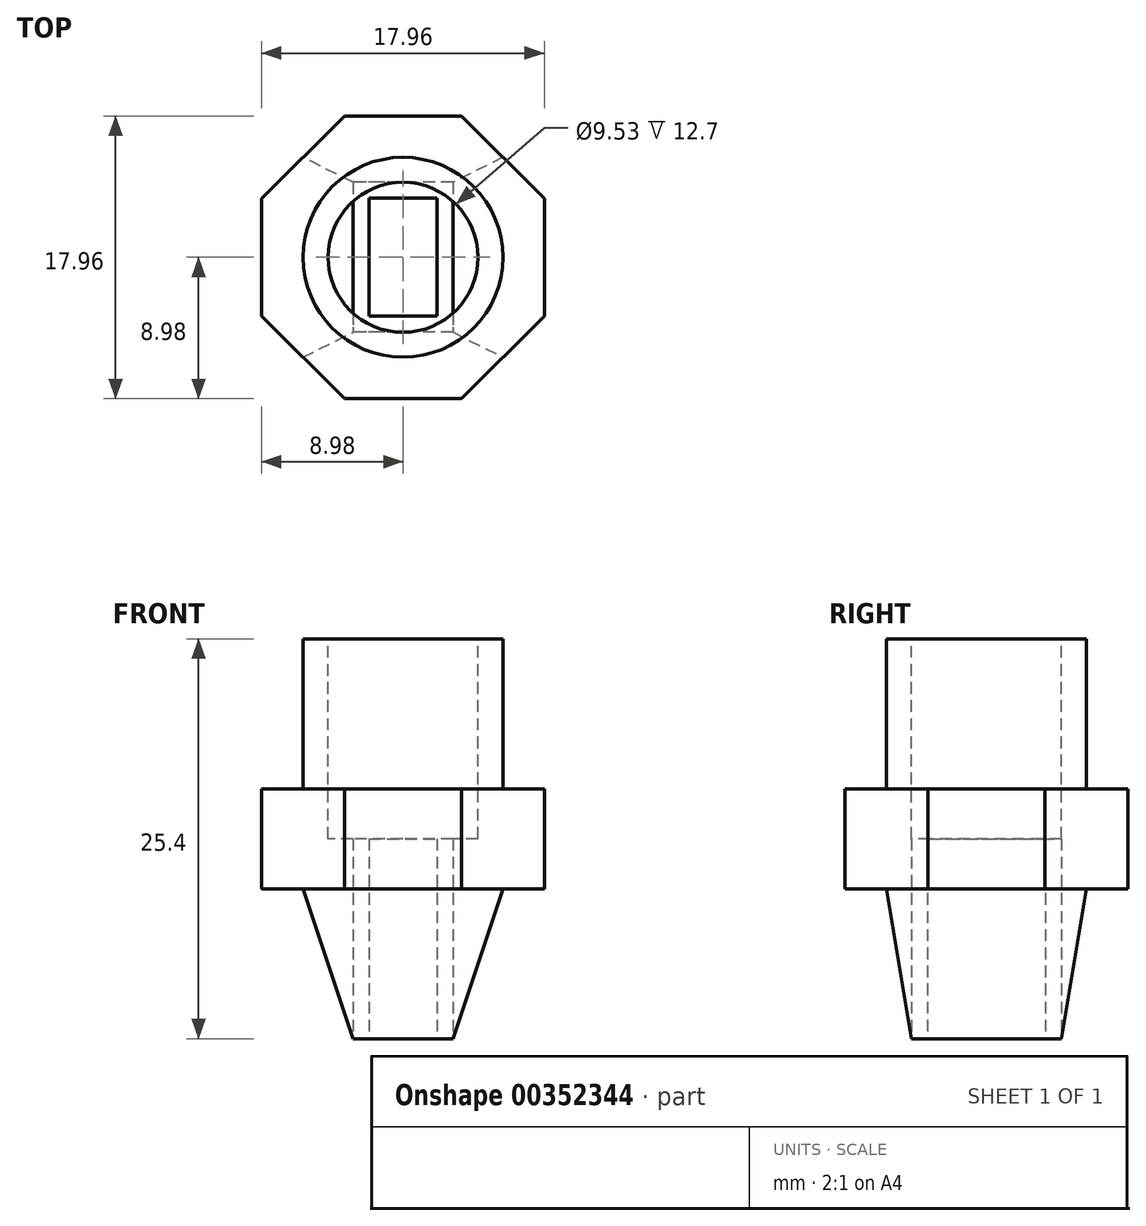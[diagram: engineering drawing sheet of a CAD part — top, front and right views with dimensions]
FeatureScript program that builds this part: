
annotation { "Feature Type Name" : "Feature", "Feature Type Description" : "" }
export const myFeature = defineFeature(function(context is Context, id is Id, definition is map)
    precondition{}
    {
        {
            var Q0;
            Q0=qCreatedBy(makeId("Top.planeOp"),FACE);
            var sketch = newSketch(context, id + "F0", { "sketchPlane" : qUnion([Q0])});
            skLineSegment(sketch, "E0.bottom", {"start": v(0, 0) * mm, "end": v(12.7, 0) * mm});
            skLineSegment(sketch, "E0.top", {"start": v(0, 12.7) * mm, "end": v(12.7, 12.7) * mm});
            skLineSegment(sketch, "E0.left", {"start": v(0, 0) * mm, "end": v(0, 12.7) * mm});
            skLineSegment(sketch, "E0.right", {"start": v(12.7, 0) * mm, "end": v(12.7, 12.7) * mm});
            skSolve(sketch);
        }
        {
            var Q0;
            Q0 = qSketchRegion(id + "F0", true);
            extrude(context, id + "F1", {"entities" : qUnion([Q0]), "depth" : 25.4 * mm});
        }
        {
            var Q0;
            Q0=makeQuery(id+"F1.opExtrude","SWEPT_FACE",FACE,{"disambiguationData":[OSD([sQuery(id+"F0.wireOp",EDGE,"E0.bottom")])]});
            var sketch = newSketch(context, id + "F2", { "sketchPlane" : qUnion([Q0])});
            skLineSegment(sketch, "E1", {"start": v(3.18, 0) * mm, "end": v(0, 9.53) * mm});
            skLineSegment(sketch, "E2", {"start": v(0, 9.53) * mm, "end": v(12.7, 9.53) * mm, "construction": true});
            skLineSegment(sketch, "E3", {"start": v(12.7, 9.53) * mm, "end": v(9.53, 0) * mm});
            skLineSegment(sketch, "E4", {"start": v(0, 0) * mm, "end": v(3.18, 0) * mm});
            skLineSegment(sketch, "E5", {"start": v(9.53, 0) * mm, "end": v(12.7, 0) * mm});
            skLineSegment(sketch, "E6", {"start": v(0, 9.53) * mm, "end": v(0, 0) * mm});
            skLineSegment(sketch, "E7", {"start": v(12.7, 0) * mm, "end": v(12.7, 9.53) * mm});
            skSolve(sketch);
        }
        {
            var Q0;
            Q0 = qSketchRegion(id + "F2", true);
            extrude(context, id + "F3", {"entities" : qUnion([Q0]), "operationType" : NewBodyOperationType.REMOVE, "endBound" : BoundingType.THROUGH_ALL, "oppositeDirection" : true, "depth" : 25.4 * mm});
        }
        {
            var Q0;
            Q0=makeQuery(id+"F1.opExtrude","SWEPT_FACE",FACE,{"disambiguationData":[OSD([sQuery(id+"F0.wireOp",EDGE,"E0.left")])]});
            var sketch = newSketch(context, id + "F4", { "sketchPlane" : qUnion([Q0])});
            skLineSegment(sketch, "E8", {"start": v(-12.7, 9.53) * mm, "end": v(-11.11, 0) * mm});
            skLineSegment(sketch, "E9", {"start": v(-11.11, 0) * mm, "end": v(-12.7, 0) * mm});
            skLineSegment(sketch, "E10", {"start": v(-12.7, 0) * mm, "end": v(-12.7, 9.53) * mm});
            skLineSegment(sketch, "E11", {"start": v(0, 9.53) * mm, "end": v(0, 0) * mm});
            skLineSegment(sketch, "E12", {"start": v(0, 0) * mm, "end": v(-1.59, 0) * mm});
            skLineSegment(sketch, "E13", {"start": v(-1.59, 0) * mm, "end": v(0, 9.53) * mm});
            skSolve(sketch);
        }
        {
            var Q0;
            Q0 = qSketchRegion(id + "F4", true);
            extrude(context, id + "F5", {"entities" : qUnion([Q0]), "operationType" : NewBodyOperationType.REMOVE, "endBound" : BoundingType.THROUGH_ALL, "oppositeDirection" : true, "depth" : 25.4 * mm});
        }
        {
            var Q0;
            Q0=makeQuery(id+"F1.opExtrude","CAP_FACE",FACE,{"disambiguationData":[OSD([sQuery(id+"F0.wireOp",EDGE,"E0.bottom"),sQuery(id+"F0.wireOp",EDGE,"E0.top"),sQuery(id+"F0.wireOp",EDGE,"E0.left"),sQuery(id+"F0.wireOp",EDGE,"E0.right")])],"isStart":true});
            var sketch = newSketch(context, id + "F6", { "sketchPlane" : qUnion([Q0])});
            skLineSegment(sketch, "E14.bottom", {"start": v(4.2, -2.6) * mm, "end": v(8.5, -2.6) * mm});
            skLineSegment(sketch, "E14.top", {"start": v(4.2, -10.1) * mm, "end": v(8.5, -10.1) * mm});
            skLineSegment(sketch, "E14.left", {"start": v(4.2, -2.6) * mm, "end": v(4.2, -10.1) * mm});
            skLineSegment(sketch, "E14.right", {"start": v(8.5, -2.6) * mm, "end": v(8.5, -10.1) * mm});
            skLineSegment(sketch, "E15.bottom", {"start": v(9.52, -11.11) * mm, "end": v(3.18, -11.11) * mm});
            skLineSegment(sketch, "E15.top", {"start": v(9.52, -1.59) * mm, "end": v(3.18, -1.59) * mm});
            skLineSegment(sketch, "E15.left", {"start": v(9.52, -11.11) * mm, "end": v(9.52, -1.59) * mm});
            skLineSegment(sketch, "E15.right", {"start": v(3.18, -11.11) * mm, "end": v(3.18, -1.59) * mm});
            skSolve(sketch);
        }
        {
            var Q0;
            Q0 = qSketchRegion(id + "F6", true);
            extrude(context, id + "F7", {"entities" : qUnion([Q0]), "operationType" : NewBodyOperationType.REMOVE, "endBound" : BoundingType.THROUGH_ALL, "oppositeDirection" : true, "depth" : 25.4 * mm});
        }
        {
            var Q0;
            Q0=makeQuery(id+"F7.boolean.opBoolean","SPLIT",FACE,{"disambiguationData":[TD([makeQuery(id+"F7.opExtrude","SWEPT_FACE",FACE,{"disambiguationData":[OSD([sQuery(id+"F6.wireOp",EDGE,"E14.bottom")])]})])],"derivedFrom":makeQuery(id+"F1.opExtrude","CAP_FACE",FACE,{"disambiguationData":[OSD([sQuery(id+"F0.wireOp",EDGE,"E0.bottom"),sQuery(id+"F0.wireOp",EDGE,"E0.top"),sQuery(id+"F0.wireOp",EDGE,"E0.left"),sQuery(id+"F0.wireOp",EDGE,"E0.right")])],"isStart":false})});
            var sketch = newSketch(context, id + "F8", { "sketchPlane" : qUnion([Q0])});
            skLineSegment(sketch, "E16", {"start": v(4.2, 10.1) * mm, "end": v(8.5, 2.6) * mm, "construction": true});
            skLineSegment(sketch, "E17", {"start": v(4.2, 2.6) * mm, "end": v(8.5, 10.1) * mm, "construction": true});
            skCircle(sketch, "E18.cCircle", {"center": v(6.35, 6.35) * mm, "radius": 8.98 * mm, "construction": true});
            skLineSegment(sketch, "E18.0", {"start": v(2.63, 15.33) * mm, "end": v(10.07, 15.33) * mm});
            skLineSegment(sketch, "E18.1", {"start": v(10.07, 15.33) * mm, "end": v(15.33, 10.07) * mm});
            skLineSegment(sketch, "E18.2", {"start": v(15.33, 10.07) * mm, "end": v(15.33, 2.63) * mm});
            skLineSegment(sketch, "E18.3", {"start": v(15.33, 2.63) * mm, "end": v(10.07, -2.63) * mm});
            skLineSegment(sketch, "E18.4", {"start": v(10.07, -2.63) * mm, "end": v(2.63, -2.63) * mm});
            skLineSegment(sketch, "E18.5", {"start": v(2.63, -2.63) * mm, "end": v(-2.63, 2.63) * mm});
            skLineSegment(sketch, "E18.6", {"start": v(-2.63, 2.63) * mm, "end": v(-2.63, 10.07) * mm});
            skLineSegment(sketch, "E18.7", {"start": v(-2.63, 10.07) * mm, "end": v(2.63, 15.33) * mm});
            skPoint(sketch, "E18.0.midPoint", {"position": v(6.35, 15.33) * mm});
            skLineSegment(sketch, "E19.bottom", {"start": v(0, 12.7) * mm, "end": v(12.7, 12.7) * mm});
            skLineSegment(sketch, "E19.top", {"start": v(0, 0) * mm, "end": v(12.7, 0) * mm});
            skLineSegment(sketch, "E19.left", {"start": v(0, 12.7) * mm, "end": v(0, 0) * mm});
            skLineSegment(sketch, "E19.right", {"start": v(12.7, 12.7) * mm, "end": v(12.7, 0) * mm});
            skSolve(sketch);
        }
        {
            var Q0;
            {var subQ0=sQuery(id+"F8.wireOp",EDGE,"E18.6");Q0=makeQuery(id+"F8.imprint","IMPRINT",FACE,{"disambiguationData":[TD([[makeQuery(id+"F8.imprint","IMPRINT",EDGE,{"derivedFrom":subQ0}),-1.0]])]});}
            var Q1;
            {var subQ0=sQuery(id+"F8.wireOp",EDGE,"E18.0");Q1=makeQuery(id+"F8.imprint","IMPRINT",FACE,{"disambiguationData":[TD([[makeQuery(id+"F8.imprint","IMPRINT",EDGE,{"derivedFrom":subQ0}),-1.0]])]});}
            var Q2;
            {var subQ0=sQuery(id+"F8.wireOp",EDGE,"E18.2");Q2=makeQuery(id+"F8.imprint","IMPRINT",FACE,{"disambiguationData":[TD([[makeQuery(id+"F8.imprint","IMPRINT",EDGE,{"derivedFrom":subQ0}),-1.0]])]});}
            var Q3;
            {var subQ0=sQuery(id+"F8.wireOp",EDGE,"E18.4");Q3=makeQuery(id+"F8.imprint","IMPRINT",FACE,{"disambiguationData":[TD([[makeQuery(id+"F8.imprint","IMPRINT",EDGE,{"derivedFrom":subQ0}),-1.0]])]});}
            extrude(context, id + "F9", {"entities" : qUnion([Q0, Q1, Q2, Q3]), "operationType" : NewBodyOperationType.ADD, "oppositeDirection" : true, "depth" : 15.88 * mm});
        }
        {
            var Q0;
            {var subQ0=sQuery(id+"F8.wireOp",EDGE,"E18.7");var subQ1=sQuery(id+"F8.wireOp",EDGE,"E18.5");var subQ2=sQuery(id+"F8.wireOp",EDGE,"E18.3");var subQ3=sQuery(id+"F8.wireOp",EDGE,"E18.1");var subQ4=sQuery(id+"F0.wireOp",EDGE,"E0.left");var subQ5=sQuery(id+"F0.wireOp",EDGE,"E0.top");var subQ6=sQuery(id+"F0.wireOp",EDGE,"E0.right");var subQ7=sQuery(id+"F0.wireOp",EDGE,"E0.bottom");Q0=makeQuery(id+"F9.boolean.opBoolean","MERGE",FACE,{"derivedFrom":[makeQuery(id+"F7.boolean.opBoolean","SPLIT",FACE,{"disambiguationData":[TD([makeQuery(id+"F1.opExtrude","SWEPT_FACE",FACE,{"disambiguationData":[OSD([subQ7])]})])],"derivedFrom":makeQuery(id+"F1.opExtrude","CAP_FACE",FACE,{"disambiguationData":[OSD([subQ7,subQ5,subQ4,subQ6])],"isStart":false})}),makeQuery(id+"F9.opExtrude","CAP_FACE",FACE,{"disambiguationData":[OSD([sQuery(id+"F8.wireOp",EDGE,"E18.0"),subQ3,subQ0,sQuery(id+"F8.wireOp",EDGE,"E19.bottom")])],"isStart":true}),makeQuery(id+"F9.opExtrude","CAP_FACE",FACE,{"disambiguationData":[OSD([subQ3,sQuery(id+"F8.wireOp",EDGE,"E18.2"),subQ2,sQuery(id+"F8.wireOp",EDGE,"E19.right")])],"isStart":true}),makeQuery(id+"F9.opExtrude","CAP_FACE",FACE,{"disambiguationData":[OSD([subQ2,sQuery(id+"F8.wireOp",EDGE,"E18.4"),subQ1,sQuery(id+"F8.wireOp",EDGE,"E19.top")])],"isStart":true}),makeQuery(id+"F9.opExtrude","CAP_FACE",FACE,{"disambiguationData":[OSD([subQ1,sQuery(id+"F8.wireOp",EDGE,"E18.6"),subQ0,sQuery(id+"F8.wireOp",EDGE,"E19.left")])],"isStart":true})]});}
            var sketch = newSketch(context, id + "F10", { "sketchPlane" : qUnion([Q0])});
            skLineSegment(sketch, "E20.0", {"start": v(-2.63, 10.07) * mm, "end": v(2.63, 15.33) * mm});
            skLineSegment(sketch, "E21.0", {"start": v(2.63, 15.33) * mm, "end": v(10.07, 15.33) * mm});
            skLineSegment(sketch, "E22.0", {"start": v(10.07, 15.33) * mm, "end": v(15.33, 10.07) * mm});
            skLineSegment(sketch, "E23.0", {"start": v(-2.63, 2.63) * mm, "end": v(-2.63, 10.07) * mm});
            skLineSegment(sketch, "E24.0", {"start": v(2.63, -2.63) * mm, "end": v(-2.63, 2.63) * mm});
            skLineSegment(sketch, "E25.0", {"start": v(10.07, -2.63) * mm, "end": v(2.63, -2.63) * mm});
            skLineSegment(sketch, "E26.0", {"start": v(15.33, 2.63) * mm, "end": v(10.07, -2.63) * mm});
            skLineSegment(sketch, "E27.0", {"start": v(15.33, 10.07) * mm, "end": v(15.33, 2.63) * mm});
            skCircle(sketch, "E28", {"center": v(6.35, 6.35) * mm, "radius": 6.35 * mm});
            skLineSegment(sketch, "E29", {"start": v(3.17, 11.11) * mm, "end": v(9.53, 1.59) * mm, "construction": true});
            skLineSegment(sketch, "E30", {"start": v(9.52, 11.11) * mm, "end": v(3.18, 1.59) * mm, "construction": true});
            skSolve(sketch);
        }
        {
            var Q0;
            {var subQ0=sQuery(id+"F10.wireOp",EDGE,"E24.0");var subQ1=sQuery(id+"F10.wireOp",EDGE,"E23.0");var subQ2=makeQuery(id+"F10.imprint","INTERSECT",VERTEX,{"derivedFrom":[subQ1,subQ0]});Q0=makeQuery(id+"F10.imprint","IMPRINT",FACE,{"disambiguationData":[TD([[makeQuery(id+"F10.imprint","IMPRINT",EDGE,{"disambiguationData":[TD([[subQ2,-1.0]])],"derivedFrom":subQ1}),-1.0]])]});}
            var Q1;
            {var subQ0=sQuery(id+"F10.wireOp",EDGE,"E25.0");var subQ1=sQuery(id+"F10.wireOp",EDGE,"E24.0");var subQ2=makeQuery(id+"F10.imprint","INTERSECT",VERTEX,{"derivedFrom":[subQ1,subQ0]});Q1=makeQuery(id+"F10.imprint","IMPRINT",FACE,{"disambiguationData":[TD([[makeQuery(id+"F10.imprint","IMPRINT",EDGE,{"disambiguationData":[TD([[subQ2,-1.0]])],"derivedFrom":subQ1}),-1.0]])]});}
            var Q2;
            {var subQ0=sQuery(id+"F10.wireOp",EDGE,"E26.0");var subQ1=sQuery(id+"F10.wireOp",EDGE,"E25.0");var subQ2=makeQuery(id+"F10.imprint","INTERSECT",VERTEX,{"derivedFrom":[subQ1,subQ0]});Q2=makeQuery(id+"F10.imprint","IMPRINT",FACE,{"disambiguationData":[TD([[makeQuery(id+"F10.imprint","IMPRINT",EDGE,{"disambiguationData":[TD([[subQ2,-1.0]])],"derivedFrom":subQ1}),-1.0]])]});}
            var Q3;
            {var subQ0=sQuery(id+"F10.wireOp",EDGE,"E27.0");var subQ1=sQuery(id+"F10.wireOp",EDGE,"E26.0");var subQ2=makeQuery(id+"F10.imprint","INTERSECT",VERTEX,{"derivedFrom":[subQ1,subQ0]});Q3=makeQuery(id+"F10.imprint","IMPRINT",FACE,{"disambiguationData":[TD([[makeQuery(id+"F10.imprint","IMPRINT",EDGE,{"disambiguationData":[TD([[subQ2,-1.0]])],"derivedFrom":subQ1}),-1.0]])]});}
            var Q4;
            {var subQ0=sQuery(id+"F10.wireOp",EDGE,"E27.0");var subQ1=sQuery(id+"F10.wireOp",EDGE,"E22.0");var subQ2=makeQuery(id+"F10.imprint","INTERSECT",VERTEX,{"derivedFrom":[subQ1,subQ0]});Q4=makeQuery(id+"F10.imprint","IMPRINT",FACE,{"disambiguationData":[TD([[makeQuery(id+"F10.imprint","IMPRINT",EDGE,{"disambiguationData":[TD([[subQ2,1.0]])],"derivedFrom":subQ1}),-1.0]])]});}
            var Q5;
            {var subQ0=sQuery(id+"F10.wireOp",EDGE,"E22.0");var subQ1=sQuery(id+"F10.wireOp",EDGE,"E21.0");var subQ2=makeQuery(id+"F10.imprint","INTERSECT",VERTEX,{"derivedFrom":[subQ1,subQ0]});Q5=makeQuery(id+"F10.imprint","IMPRINT",FACE,{"disambiguationData":[TD([[makeQuery(id+"F10.imprint","IMPRINT",EDGE,{"disambiguationData":[TD([[subQ2,1.0]])],"derivedFrom":subQ1}),-1.0]])]});}
            var Q6;
            {var subQ0=sQuery(id+"F10.wireOp",EDGE,"E21.0");var subQ1=sQuery(id+"F10.wireOp",EDGE,"E20.0");var subQ2=makeQuery(id+"F10.imprint","INTERSECT",VERTEX,{"derivedFrom":[subQ1,subQ0]});Q6=makeQuery(id+"F10.imprint","IMPRINT",FACE,{"disambiguationData":[TD([[makeQuery(id+"F10.imprint","IMPRINT",EDGE,{"disambiguationData":[TD([[subQ2,1.0]])],"derivedFrom":subQ1}),-1.0]])]});}
            var Q7;
            {var subQ0=sQuery(id+"F10.wireOp",EDGE,"E23.0");var subQ1=sQuery(id+"F10.wireOp",EDGE,"E20.0");var subQ2=makeQuery(id+"F10.imprint","INTERSECT",VERTEX,{"derivedFrom":[subQ1,subQ0]});Q7=makeQuery(id+"F10.imprint","IMPRINT",FACE,{"disambiguationData":[TD([[makeQuery(id+"F10.imprint","IMPRINT",EDGE,{"disambiguationData":[TD([[subQ2,-1.0]])],"derivedFrom":subQ1}),-1.0]])]});}
            extrude(context, id + "F11", {"entities" : qUnion([Q0, Q1, Q2, Q3, Q4, Q5, Q6, Q7]), "operationType" : NewBodyOperationType.REMOVE, "oppositeDirection" : true, "depth" : 9.52 * mm});
        }
        {
            var Q0;
            {var subQ0=sQuery(id+"F8.wireOp",EDGE,"E18.7");var subQ1=sQuery(id+"F8.wireOp",EDGE,"E18.5");var subQ2=sQuery(id+"F8.wireOp",EDGE,"E18.3");var subQ3=sQuery(id+"F8.wireOp",EDGE,"E18.1");var subQ4=sQuery(id+"F0.wireOp",EDGE,"E0.left");var subQ5=sQuery(id+"F0.wireOp",EDGE,"E0.top");var subQ6=sQuery(id+"F0.wireOp",EDGE,"E0.right");var subQ7=sQuery(id+"F0.wireOp",EDGE,"E0.bottom");Q0=makeQuery(id+"F9.boolean.opBoolean","MERGE",FACE,{"derivedFrom":[makeQuery(id+"F7.boolean.opBoolean","SPLIT",FACE,{"disambiguationData":[TD([makeQuery(id+"F1.opExtrude","SWEPT_FACE",FACE,{"disambiguationData":[OSD([subQ7])]})])],"derivedFrom":makeQuery(id+"F1.opExtrude","CAP_FACE",FACE,{"disambiguationData":[OSD([subQ7,subQ5,subQ4,subQ6])],"isStart":false})}),makeQuery(id+"F9.opExtrude","CAP_FACE",FACE,{"disambiguationData":[OSD([sQuery(id+"F8.wireOp",EDGE,"E18.0"),subQ3,subQ0,sQuery(id+"F8.wireOp",EDGE,"E19.bottom")])],"isStart":true}),makeQuery(id+"F9.opExtrude","CAP_FACE",FACE,{"disambiguationData":[OSD([subQ3,sQuery(id+"F8.wireOp",EDGE,"E18.2"),subQ2,sQuery(id+"F8.wireOp",EDGE,"E19.right")])],"isStart":true}),makeQuery(id+"F9.opExtrude","CAP_FACE",FACE,{"disambiguationData":[OSD([subQ2,sQuery(id+"F8.wireOp",EDGE,"E18.4"),subQ1,sQuery(id+"F8.wireOp",EDGE,"E19.top")])],"isStart":true}),makeQuery(id+"F9.opExtrude","CAP_FACE",FACE,{"disambiguationData":[OSD([subQ1,sQuery(id+"F8.wireOp",EDGE,"E18.6"),subQ0,sQuery(id+"F8.wireOp",EDGE,"E19.left")])],"isStart":true})]});}
            var sketch = newSketch(context, id + "F12", { "sketchPlane" : qUnion([Q0])});
            skCircle(sketch, "E31.0", {"center": v(6.35, 6.35) * mm, "radius": 6.35 * mm});
            skCircle(sketch, "E32", {"center": v(6.35, 6.35) * mm, "radius": 4.76 * mm});
            skSolve(sketch);
        }
        {
            var Q0;
            Q0 = qSketchRegion(id + "F12", true);
            extrude(context, id + "F13", {"entities" : qUnion([Q0]), "operationType" : NewBodyOperationType.ADD, "oppositeDirection" : true, "depth" : 12.7 * mm});
        }
        {
            var Q0;
            Q0=makeQuery(id+"F7.boolean.opBoolean","SPLIT",FACE,{"disambiguationData":[TD([makeQuery(id+"F7.opExtrude","SWEPT_FACE",FACE,{"disambiguationData":[OSD([sQuery(id+"F6.wireOp",EDGE,"E14.bottom")])]})])],"derivedFrom":makeQuery(id+"F1.opExtrude","CAP_FACE",FACE,{"disambiguationData":[OSD([sQuery(id+"F0.wireOp",EDGE,"E0.bottom"),sQuery(id+"F0.wireOp",EDGE,"E0.top"),sQuery(id+"F0.wireOp",EDGE,"E0.left"),sQuery(id+"F0.wireOp",EDGE,"E0.right")])],"isStart":false})});
            var sketch = newSketch(context, id + "F14", { "sketchPlane" : qUnion([Q0])});
            skCircle(sketch, "E33.0", {"center": v(6.35, 6.35) * mm, "radius": 6.35 * mm});
            skCircle(sketch, "E34", {"center": v(6.35, 6.35) * mm, "radius": 4.76 * mm});
            skSolve(sketch);
        }
        {
            var Q0;
            Q0=makeQuery(id+"F14.imprint","IMPRINT",FACE,{"disambiguationData":[TD([[makeQuery(id+"F14.imprint","IMPRINT",EDGE,{"derivedFrom":sQuery(id+"F14.wireOp",EDGE,"E34")}),1.0]])]});
            var Q1;
            {var subQ0=makeQuery(id+"F1.opExtrude","CAP_FACE",FACE,{"disambiguationData":[OSD([sQuery(id+"F0.wireOp",EDGE,"E0.bottom"),sQuery(id+"F0.wireOp",EDGE,"E0.top"),sQuery(id+"F0.wireOp",EDGE,"E0.left"),sQuery(id+"F0.wireOp",EDGE,"E0.right")])],"isStart":false});Q1=makeQuery(id+"F14.imprint","IMPRINT",FACE,{"disambiguationData":[TD([[makeQuery(id+"F14.imprint","IMPRINT",EDGE,{"derivedFrom":makeQuery(id+"F7.boolean.opBoolean","INTERSECT",EDGE,{"derivedFrom":[subQ0,makeQuery(id+"F7.opExtrude","SWEPT_FACE",FACE,{"disambiguationData":[OSD([sQuery(id+"F6.wireOp",EDGE,"E14.bottom")])]})]})}),-1.0]])]});}
            extrude(context, id + "F15", {"entities" : qUnion([Q0, Q1]), "operationType" : NewBodyOperationType.REMOVE, "oppositeDirection" : true, "depth" : 12.7 * mm});
        }
    });
